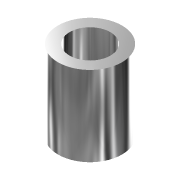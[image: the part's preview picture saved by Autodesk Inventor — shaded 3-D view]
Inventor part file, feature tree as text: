
AUTODESK INVENTOR PART (.ipt)
format: ipt  version: 2012 (Build 160160000, 160)  size: 81,408 bytes
history: native  units: mm
features: extrude x1, sketch x1
ambient origin geometry x8: Origin, YZ Plane, XZ Plane, XY Plane, X Axis, Y Axis, Z Axis, Center Point
bodies: Solid1 (feature_tree)
feature tree (2):
  extrude  "Extrusion1"  Depth=5.1mm
  sketch  "Sketch1"  dims[d0=8.0mm d1=5.1mm d2=10.0mm d3=0.0mm]
